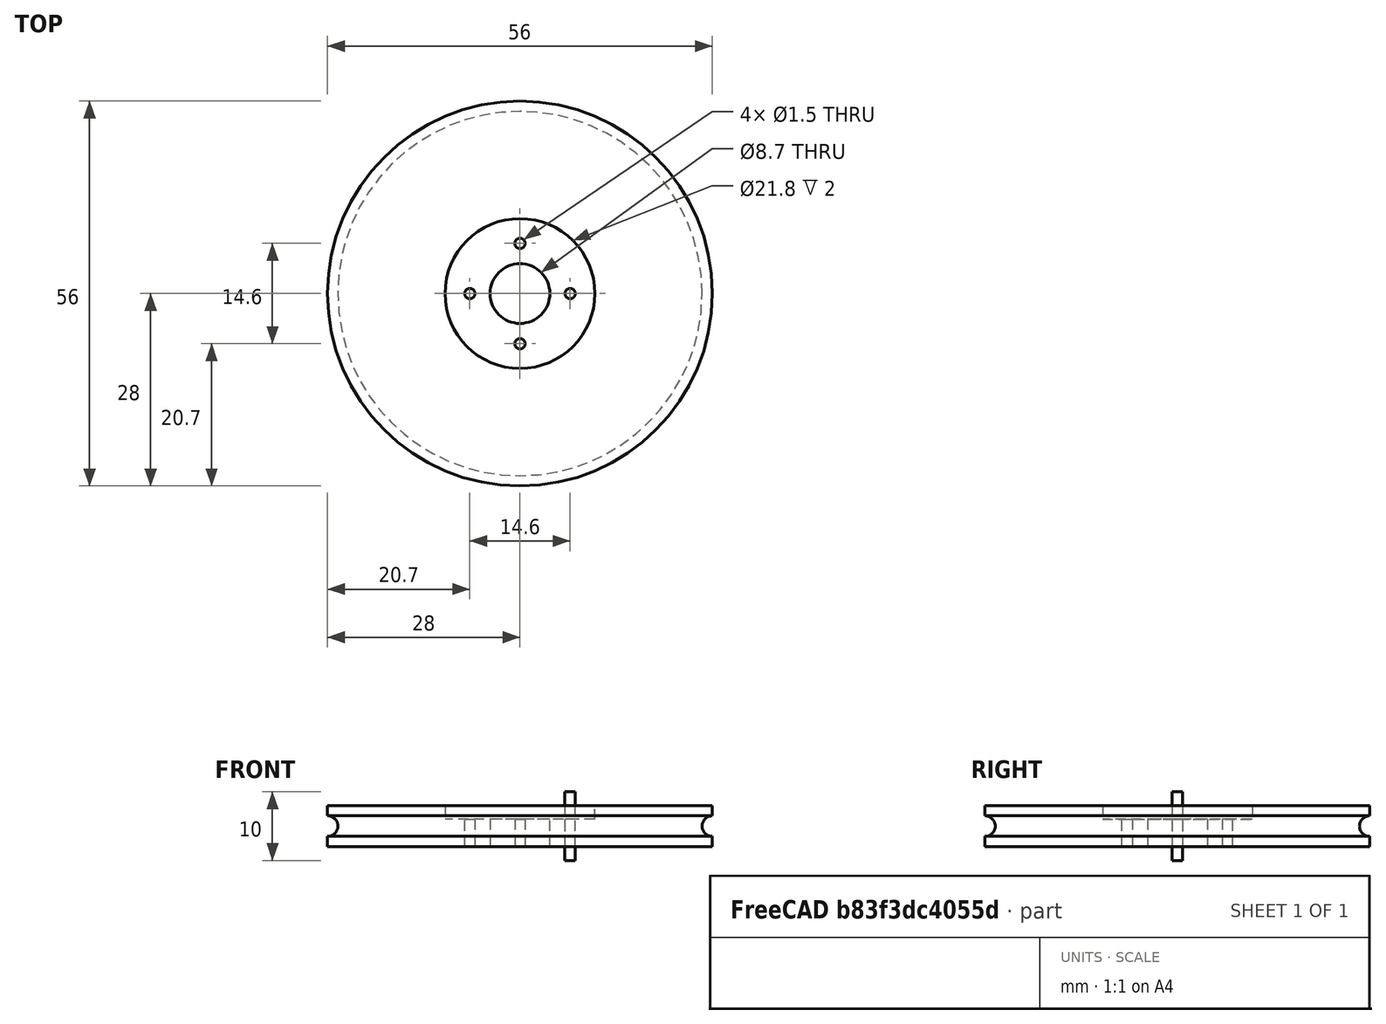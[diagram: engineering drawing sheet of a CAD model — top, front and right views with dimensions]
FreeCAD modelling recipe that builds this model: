
FCSTD DOCUMENT  (FreeCAD 0.21R33694 (Git))
Label: OJT1_T15P01.roda_algo
License: All rights reserved
LicenseURL: http://en.wikipedia.org/wiki/All_rights_reserved
objects: Part::Cylinder×4, Part::Cut×4, Part::Torus×1, Part::FeaturePython×1
note: 9 computed .brp shape members not serialized (recipe doc carries the construction recipe); baked Part::Feature solids carry a one-line shape summary decoded from their .brp

FEATURE [Part::Cylinder] Cylinder  label="Cilindre"
  Angle = 360
  AttacherType = Attacher::AttachEngine3D
  FirstAngle = 0
  Height = 6
  Radius = 28
  SecondAngle = 0
FEATURE [Part::Torus] Torus
  Angle1 = -180
  Angle2 = 180
  Angle3 = 360
  AttacherType = Attacher::AttachEngine3D
  Placement = pos=(0,0,3) rot=(0,0,1;0rad)
  Radius1 = 28
  Radius2 = 1.5
FEATURE [Part::Cut] Cut
  Base = -> Cylinder
  Refine = true
  Tool = -> Torus
FEATURE [Part::Cylinder] Cylinder001  label="Cilindre001"
  Angle = 360
  AttacherType = Attacher::AttachEngine3D
  FirstAngle = 0
  Height = 10
  Placement = pos=(0,0,4) rot=(0,0,1;0rad)
  Radius = 10.9
  SecondAngle = 0
FEATURE [Part::Cut] Cut001
  Base = -> Cut
  Refine = true
  Tool = -> Cylinder001
FEATURE [Part::Cylinder] Cylinder002  label="Cilindre002"
  Angle = 360
  AttacherType = Attacher::AttachEngine3D
  FirstAngle = 0
  Height = 10
  Placement = pos=(0,0,-4) rot=(0,0,1;0rad)
  Radius = 4.35
  SecondAngle = 0
FEATURE [Part::Cut] Cut002
  Base = -> Cut001
  Refine = true
  Tool = -> Cylinder002
FEATURE [Part::Cylinder] Cylinder003  label="Cilindre003"
  Angle = 360
  AttacherType = Attacher::AttachEngine3D
  FirstAngle = 0
  Height = 10
  Placement = pos=(7.3,0,-2) rot=(0,0,1;0rad)
  Radius = 0.75
  SecondAngle = 0
FEATURE [Part::FeaturePython] Array  # Draft array (typed FeaturePython)
  AlwaysSyncPlacement = false
  Angle = 360
  ArrayType = 1
  Axis = (0,0,1)
  Base = -> Cylinder003
  Center = (0,0,0)
  Count = 4
  ExpandArray = false
  Fuse = false
  IntervalAxis = (0,0,0)
  IntervalX = (50,0,0)
  IntervalY = (0,50,0)
  IntervalZ = (0,0,50)
  NumberCircles = 3
  NumberPolar = 4
  NumberX = 2
  NumberY = 2
  NumberZ = 1
  PlacementList = 4 placements: [(7.3,0,-2),(0,7.3,-2),(-7.3,8.93992e-16,-2),(-1.62093e-15,-7.3,-2)]
  RadialDistance = 50
  ScaleList = (4) [(1,1,1),(1,1,1),(1,1,1),(1,1,1)]
  Symmetry = 1
  TangentialDistance = 25
FEATURE [Part::Cut] Cut003
  Base = -> Cut002
  Refine = true
  Tool = -> Array
